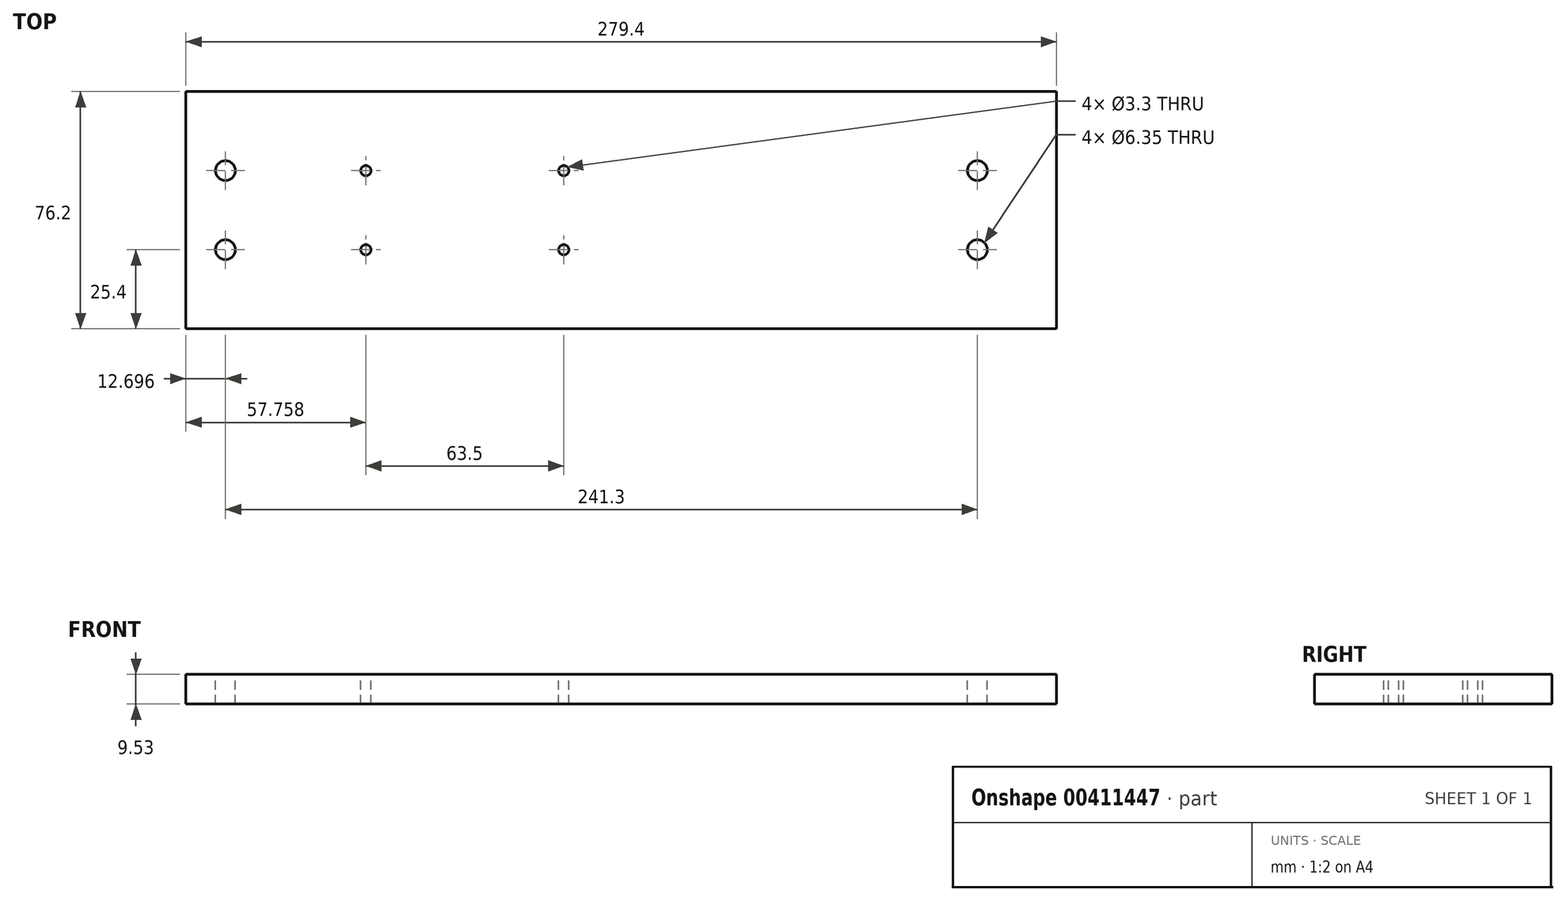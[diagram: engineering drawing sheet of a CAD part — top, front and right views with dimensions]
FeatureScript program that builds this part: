
annotation { "Feature Type Name" : "Feature", "Feature Type Description" : "" }
export const myFeature = defineFeature(function(context is Context, id is Id, definition is map)
    precondition{}
    {
        {
            var Q0;
            Q0=qCreatedBy(makeId("Top.planeOp"),FACE);
            var sketch = newSketch(context, id + "F0", { "sketchPlane" : qUnion([Q0])});
            skLineSegment(sketch, "E0.bottom", {"start": v(-140.04, 38.1) * mm, "end": v(139.36, 38.1) * mm});
            skLineSegment(sketch, "E0.top", {"start": v(-140.04, -38.1) * mm, "end": v(139.36, -38.1) * mm});
            skLineSegment(sketch, "E0.left", {"start": v(-140.04, 38.1) * mm, "end": v(-140.04, -38.1) * mm});
            skLineSegment(sketch, "E0.right", {"start": v(139.36, 38.1) * mm, "end": v(139.36, -38.1) * mm});
            skCircle(sketch, "E1", {"center": v(-82.28, 12.7) * mm, "radius": 1.65 * mm});
            skCircle(sketch, "E2.1.0.0", {"center": v(-18.78, 12.7) * mm, "radius": 1.65 * mm});
            skLineSegment(sketch, "E2.direction1", {"start": v(-82.28, 12.7) * mm, "end": v(-18.78, 12.7) * mm, "construction": true});
            skCircle(sketch, "E3.MirrorC", {"center": v(-18.78, -12.7) * mm, "radius": 1.65 * mm});
            skCircle(sketch, "E4.MirrorC", {"center": v(-82.28, -12.7) * mm, "radius": 1.65 * mm});
            skCircle(sketch, "E5", {"center": v(-127.34, 12.7) * mm, "radius": 3.18 * mm});
            skCircle(sketch, "E6", {"center": v(-127.34, -12.7) * mm, "radius": 3.17 * mm});
            skCircle(sketch, "E7", {"center": v(113.96, 12.7) * mm, "radius": 3.18 * mm});
            skCircle(sketch, "E8", {"center": v(113.96, -12.7) * mm, "radius": 3.17 * mm});
            skSolve(sketch);
        }
        {
            var Q0;
            Q0=makeQuery(id+"F0.imprint","IMPRINT",FACE,{"disambiguationData":[TD([[makeQuery(id+"F0.imprint","IMPRINT",EDGE,{"derivedFrom":sQuery(id+"F0.wireOp",EDGE,"E0.bottom")}),-1.0]])]});
            extrude(context, id + "F1", {"entities" : qUnion([Q0]), "oppositeDirection" : true, "depth" : 9.52 * mm});
        }
    });
